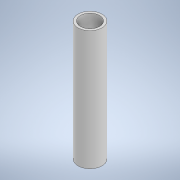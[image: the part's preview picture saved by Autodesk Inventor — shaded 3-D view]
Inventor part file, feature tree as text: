
AUTODESK INVENTOR PART (.ipt)
format: ipt  version: 2020 (Build 240168000, 168)  size: 95,232 bytes
history: native  units: mm
features: extrude x1, sketch x1
ambient origin geometry x8: Origin, YZ Plane, XZ Plane, XY Plane, X Axis, Y Axis, Z Axis, Center Point
bodies: Solid1 (feature_tree)
feature tree (2):
  extrude  "Extrusion1"  Depth=100.0mm
  sketch  "Sketch1"  dims[d0=20.0mm d1=2.0mm d2=100.0mm d3=0.0mm]
